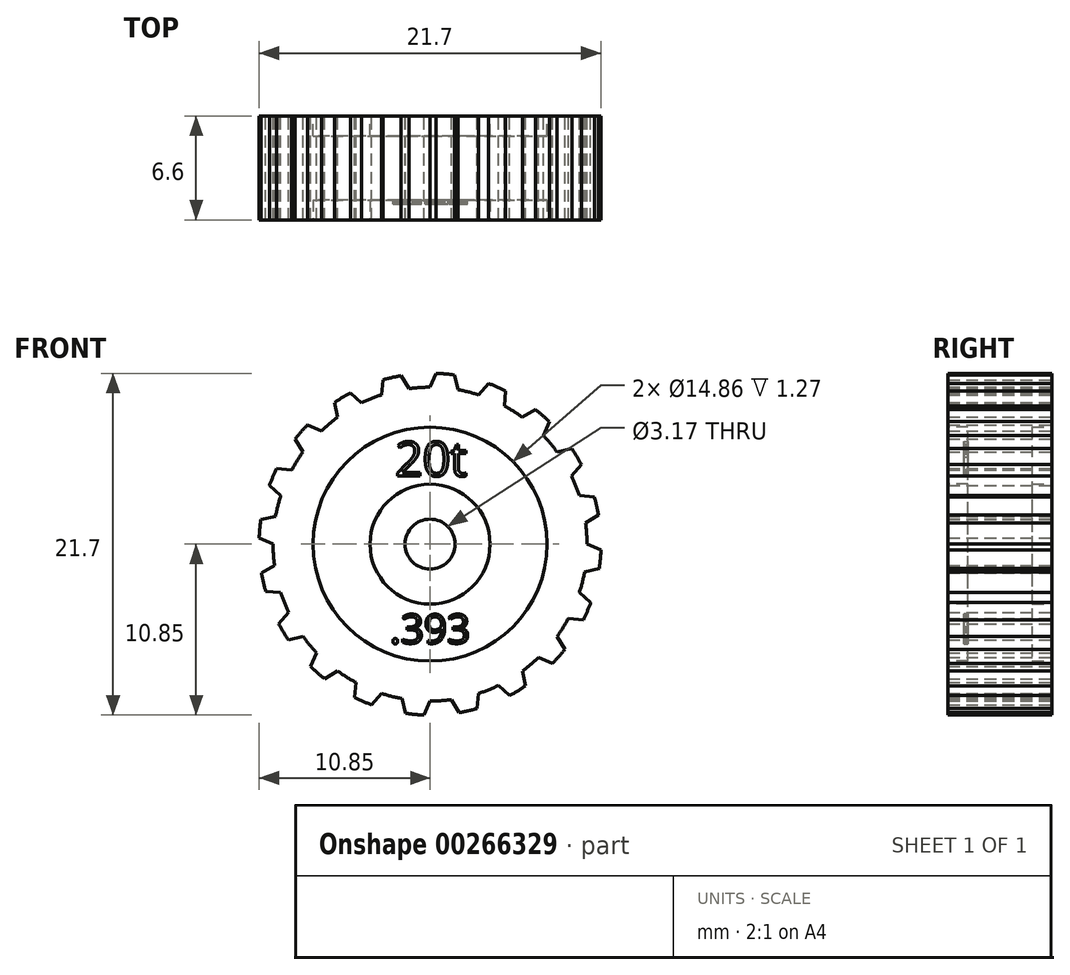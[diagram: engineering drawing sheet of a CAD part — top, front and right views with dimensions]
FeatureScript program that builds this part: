
annotation { "Feature Type Name" : "Feature", "Feature Type Description" : "" }
export const myFeature = defineFeature(function(context is Context, id is Id, definition is map)
    precondition{}
    {
        {
            var Q0;
            Q0=qCreatedBy(makeId("Front.planeOp"),FACE);
            var sketch = newSketch(context, id + "F0", { "sketchPlane" : qUnion([Q0])});
            skCircle(sketch, "E0", {"center": v(0, 0) * mm, "radius": 9.97 * mm});
            skCircle(sketch, "E1", {"center": v(0, 0) * mm, "radius": 1.59 * mm});
            skSolve(sketch);
        }
        {
            var Q0;
            Q0=qSketchRegion(id+"F0",true);
            extrude(context, id + "F1", {"entities" : qUnion([Q0]), "depth" : 6.6 * mm, "offsetDistance" : 25.4 * mm});
        }
        {
            var Q0;
            Q0=makeQuery(id+"F1.opExtrude","CAP_FACE",FACE,{"disambiguationData":[OSD([sQuery(id+"F0.wireOp",EDGE,"E0"),sQuery(id+"F0.wireOp",EDGE,"E1")])],"isStart":false});
            var sketch = newSketch(context, id + "F2", { "sketchPlane" : qUnion([Q0])});
            skCircle(sketch, "E2.0", {"center": v(0, 0) * mm, "radius": 7.43 * mm});
            skCircle(sketch, "E3", {"center": v(0, 0) * mm, "radius": 3.81 * mm});
            skSolve(sketch);
        }
        {
            var Q0;
            Q0=qSketchRegion(id+"F2",true);
            extrude(context, id + "F3", {"entities" : qUnion([Q0]), "operationType" : NewBodyOperationType.REMOVE, "oppositeDirection" : true, "depth" : 1.27 * mm});
        }
        {
            var Q0;
            Q0=makeQuery(id+"F1.opExtrude","CAP_FACE",FACE,{"disambiguationData":[OSD([sQuery(id+"F0.wireOp",EDGE,"E0"),sQuery(id+"F0.wireOp",EDGE,"E1")])],"isStart":true});
            var sketch = newSketch(context, id + "F4", { "sketchPlane" : qUnion([Q0])});
            skCircle(sketch, "E4.0", {"center": v(0, 0) * mm, "radius": 7.43 * mm});
            skCircle(sketch, "E5", {"center": v(0, 0) * mm, "radius": 3.81 * mm});
            skSolve(sketch);
        }
        {
            var Q0;
            Q0=qSketchRegion(id+"F4",true);
            extrude(context, id + "F5", {"entities" : qUnion([Q0]), "operationType" : NewBodyOperationType.REMOVE, "oppositeDirection" : true, "depth" : 1.27 * mm});
        }
        {
            var Q0;
            Q0=makeQuery(id+"F3.boolean.opBoolean","COPY",FACE,{"derivedFrom":makeQuery(id+"F3.opExtrude","CAP_FACE",FACE,{"disambiguationData":[OSD([sQuery(id+"F2.wireOp",EDGE,"E2.0"),sQuery(id+"F2.wireOp",EDGE,"E3")])],"isStart":false})});
            var sketch = newSketch(context, id + "F6", { "sketchPlane" : qUnion([Q0])});
            skText(sketch, "E6", { "text": "20t", "fontName": "OpenSans-Regular.ttf"});
            skText(sketch, "E7", { "text": ".393", "fontName": "OpenSans-Regular.ttf"});
            const initialGuessF6  = {"E6": [-0.00221, 0.00432, 1, 0, 0.0022], "E7": [-0.00255, -0.0063, 1, 0, 0.00185]};
            skSetInitialGuess(sketch, initialGuessF6);
            skSolve(sketch);
        }
        {
            var Q0;
            Q0=qSketchRegion(id+"F6",true);
            extrude(context, id + "F7", {"entities" : qUnion([Q0]), "operationType" : NewBodyOperationType.ADD, "depth" : 0.25 * mm});
        }
        {
            var Q0;
            {var subQ0=sQuery(id+"F0.wireOp",EDGE,"E0");Q0=makeQuery(id+"F5.boolean.opBoolean","SPLIT",FACE,{"disambiguationData":[TD([makeQuery(id+"F1.opExtrude","SWEPT_FACE",FACE,{"disambiguationData":[OSD([subQ0])]})])],"derivedFrom":makeQuery(id+"F1.opExtrude","CAP_FACE",FACE,{"disambiguationData":[OSD([subQ0,sQuery(id+"F0.wireOp",EDGE,"E1")])],"isStart":true})});}
            var sketch = newSketch(context, id + "F8", { "sketchPlane" : qUnion([Q0])});
            skLineSegment(sketch, "E8", {"start": v(0, 0) * mm, "end": v(0, 11.7) * mm, "construction": true});
            skLineSegment(sketch, "E9", {"start": v(0, 0) * mm, "end": v(-3.65, 11.22) * mm, "construction": true});
            skLineSegment(sketch, "E10", {"start": v(0, 0) * mm, "end": v(-1.8, 11.36) * mm, "construction": true});
            skArc(sketch, "E11", {"start": v(-0.38, 10.85) * mm, "mid": v(-0.97, 10.82) * mm, "end": v(-1.56, 10.75) * mm});
            skLineSegment(sketch, "E12", {"start": v(0, 9.97) * mm, "end": v(-0.38, 10.85) * mm});
            skLineSegment(sketch, "E13", {"start": v(-1.56, 10.75) * mm, "end": v(-1.77, 9.81) * mm});
            skLineSegment(sketch, "E14", {"start": v(-1.77, 9.81) * mm, "end": v(0, 9.97) * mm});
            skArc(sketch, "E15.1.0", {"start": v(-3.71, 10.2) * mm, "mid": v(-4.26, 9.99) * mm, "end": v(-4.8, 9.74) * mm});
            skLineSegment(sketch, "E15.1.1", {"start": v(-4.8, 9.74) * mm, "end": v(-4.71, 8.78) * mm});
            skLineSegment(sketch, "E15.1.2", {"start": v(-4.71, 8.78) * mm, "end": v(-3.08, 9.48) * mm});
            skLineSegment(sketch, "E15.1.3", {"start": v(-3.08, 9.48) * mm, "end": v(-3.71, 10.2) * mm});
            skArc(sketch, "E15.2.0", {"start": v(-6.68, 8.56) * mm, "mid": v(-7.14, 8.18) * mm, "end": v(-7.57, 7.78) * mm});
            skLineSegment(sketch, "E15.2.1", {"start": v(-7.57, 7.78) * mm, "end": v(-7.2, 6.9) * mm});
            skLineSegment(sketch, "E15.2.2", {"start": v(-7.2, 6.9) * mm, "end": v(-5.86, 8.07) * mm});
            skLineSegment(sketch, "E15.2.3", {"start": v(-5.86, 8.07) * mm, "end": v(-6.68, 8.56) * mm});
            skArc(sketch, "E16.1.3.0", {"start": v(-9, 6.07) * mm, "mid": v(-9.32, 5.57) * mm, "end": v(-9.6, 5.06) * mm});
            skLineSegment(sketch, "E16.4.3.0", {"start": v(-9.6, 5.06) * mm, "end": v(-8.98, 4.34) * mm});
            skLineSegment(sketch, "E16.7.3.0", {"start": v(-8.98, 4.34) * mm, "end": v(-8.07, 5.86) * mm});
            skLineSegment(sketch, "E16.10.3.0", {"start": v(-8.07, 5.86) * mm, "end": v(-9, 6.07) * mm});
            skArc(sketch, "E16.1.4.0", {"start": v(-10.44, 3) * mm, "mid": v(-10.59, 2.42) * mm, "end": v(-10.7, 1.84) * mm});
            skLineSegment(sketch, "E16.4.4.0", {"start": v(-10.7, 1.84) * mm, "end": v(-9.88, 1.35) * mm});
            skLineSegment(sketch, "E16.7.4.0", {"start": v(-9.88, 1.35) * mm, "end": v(-9.48, 3.08) * mm});
            skLineSegment(sketch, "E16.10.4.0", {"start": v(-9.48, 3.08) * mm, "end": v(-10.44, 3) * mm});
            skArc(sketch, "E16.1.5.0", {"start": v(-10.85, -0.38) * mm, "mid": v(-10.82, -0.97) * mm, "end": v(-10.75, -1.56) * mm});
            skLineSegment(sketch, "E16.4.5.0", {"start": v(-10.75, -1.56) * mm, "end": v(-9.81, -1.77) * mm});
            skLineSegment(sketch, "E16.7.5.0", {"start": v(-9.81, -1.77) * mm, "end": v(-9.97, 0) * mm});
            skLineSegment(sketch, "E16.10.5.0", {"start": v(-9.97, 0) * mm, "end": v(-10.85, -0.38) * mm});
            skArc(sketch, "E16.1.6.0", {"start": v(-10.2, -3.71) * mm, "mid": v(-9.99, -4.26) * mm, "end": v(-9.74, -4.8) * mm});
            skLineSegment(sketch, "E16.4.6.0", {"start": v(-9.74, -4.8) * mm, "end": v(-8.78, -4.71) * mm});
            skLineSegment(sketch, "E16.7.6.0", {"start": v(-8.78, -4.71) * mm, "end": v(-9.48, -3.08) * mm});
            skLineSegment(sketch, "E16.10.6.0", {"start": v(-9.48, -3.08) * mm, "end": v(-10.2, -3.71) * mm});
            skArc(sketch, "E16.1.7.0", {"start": v(-8.56, -6.68) * mm, "mid": v(-8.18, -7.14) * mm, "end": v(-7.78, -7.57) * mm});
            skLineSegment(sketch, "E16.4.7.0", {"start": v(-7.78, -7.57) * mm, "end": v(-6.9, -7.2) * mm});
            skLineSegment(sketch, "E16.7.7.0", {"start": v(-6.9, -7.2) * mm, "end": v(-8.07, -5.86) * mm});
            skLineSegment(sketch, "E16.10.7.0", {"start": v(-8.07, -5.86) * mm, "end": v(-8.56, -6.68) * mm});
            skArc(sketch, "E16.1.8.0", {"start": v(-6.07, -9) * mm, "mid": v(-5.57, -9.32) * mm, "end": v(-5.06, -9.6) * mm});
            skLineSegment(sketch, "E16.4.8.0", {"start": v(-5.06, -9.6) * mm, "end": v(-4.34, -8.98) * mm});
            skLineSegment(sketch, "E16.7.8.0", {"start": v(-4.34, -8.98) * mm, "end": v(-5.86, -8.07) * mm});
            skLineSegment(sketch, "E16.10.8.0", {"start": v(-5.86, -8.07) * mm, "end": v(-6.07, -9) * mm});
            skArc(sketch, "E16.1.9.0", {"start": v(-3, -10.44) * mm, "mid": v(-2.42, -10.59) * mm, "end": v(-1.84, -10.7) * mm});
            skLineSegment(sketch, "E16.4.9.0", {"start": v(-1.84, -10.7) * mm, "end": v(-1.35, -9.88) * mm});
            skLineSegment(sketch, "E16.7.9.0", {"start": v(-1.35, -9.88) * mm, "end": v(-3.08, -9.48) * mm});
            skLineSegment(sketch, "E16.10.9.0", {"start": v(-3.08, -9.48) * mm, "end": v(-3, -10.44) * mm});
            skArc(sketch, "E16.1.10.0", {"start": v(0.38, -10.85) * mm, "mid": v(0.97, -10.82) * mm, "end": v(1.56, -10.75) * mm});
            skLineSegment(sketch, "E16.4.10.0", {"start": v(1.56, -10.75) * mm, "end": v(1.77, -9.81) * mm});
            skLineSegment(sketch, "E16.7.10.0", {"start": v(1.77, -9.81) * mm, "end": v(0, -9.97) * mm});
            skLineSegment(sketch, "E16.10.10.0", {"start": v(0, -9.97) * mm, "end": v(0.38, -10.85) * mm});
            skArc(sketch, "E16.1.11.0", {"start": v(3.71, -10.2) * mm, "mid": v(4.26, -9.99) * mm, "end": v(4.8, -9.74) * mm});
            skLineSegment(sketch, "E16.4.11.0", {"start": v(4.8, -9.74) * mm, "end": v(4.71, -8.78) * mm});
            skLineSegment(sketch, "E16.7.11.0", {"start": v(4.71, -8.78) * mm, "end": v(3.08, -9.48) * mm});
            skLineSegment(sketch, "E16.10.11.0", {"start": v(3.08, -9.48) * mm, "end": v(3.71, -10.2) * mm});
            skArc(sketch, "E16.1.12.0", {"start": v(6.68, -8.56) * mm, "mid": v(7.14, -8.18) * mm, "end": v(7.57, -7.78) * mm});
            skLineSegment(sketch, "E16.4.12.0", {"start": v(7.57, -7.78) * mm, "end": v(7.2, -6.9) * mm});
            skLineSegment(sketch, "E16.7.12.0", {"start": v(7.2, -6.9) * mm, "end": v(5.86, -8.07) * mm});
            skLineSegment(sketch, "E16.10.12.0", {"start": v(5.86, -8.07) * mm, "end": v(6.68, -8.56) * mm});
            skArc(sketch, "E16.1.13.0", {"start": v(9, -6.07) * mm, "mid": v(9.32, -5.57) * mm, "end": v(9.6, -5.06) * mm});
            skLineSegment(sketch, "E16.4.13.0", {"start": v(9.6, -5.06) * mm, "end": v(8.98, -4.34) * mm});
            skLineSegment(sketch, "E16.7.13.0", {"start": v(8.98, -4.34) * mm, "end": v(8.07, -5.86) * mm});
            skLineSegment(sketch, "E16.10.13.0", {"start": v(8.07, -5.86) * mm, "end": v(9, -6.07) * mm});
            skArc(sketch, "E16.1.14.0", {"start": v(10.44, -3) * mm, "mid": v(10.59, -2.42) * mm, "end": v(10.7, -1.84) * mm});
            skLineSegment(sketch, "E16.4.14.0", {"start": v(10.7, -1.84) * mm, "end": v(9.88, -1.35) * mm});
            skLineSegment(sketch, "E16.7.14.0", {"start": v(9.88, -1.35) * mm, "end": v(9.48, -3.08) * mm});
            skLineSegment(sketch, "E16.10.14.0", {"start": v(9.48, -3.08) * mm, "end": v(10.44, -3) * mm});
            skArc(sketch, "E16.1.15.0", {"start": v(10.85, 0.38) * mm, "mid": v(10.82, 0.97) * mm, "end": v(10.75, 1.56) * mm});
            skLineSegment(sketch, "E16.4.15.0", {"start": v(10.75, 1.56) * mm, "end": v(9.81, 1.77) * mm});
            skLineSegment(sketch, "E16.7.15.0", {"start": v(9.81, 1.77) * mm, "end": v(9.97, 0) * mm});
            skLineSegment(sketch, "E16.10.15.0", {"start": v(9.97, 0) * mm, "end": v(10.85, 0.38) * mm});
            skArc(sketch, "E16.1.16.0", {"start": v(10.2, 3.71) * mm, "mid": v(9.99, 4.26) * mm, "end": v(9.74, 4.8) * mm});
            skLineSegment(sketch, "E16.4.16.0", {"start": v(9.74, 4.8) * mm, "end": v(8.78, 4.71) * mm});
            skLineSegment(sketch, "E16.7.16.0", {"start": v(8.78, 4.71) * mm, "end": v(9.48, 3.08) * mm});
            skLineSegment(sketch, "E16.10.16.0", {"start": v(9.48, 3.08) * mm, "end": v(10.2, 3.71) * mm});
            skArc(sketch, "E16.1.17.0", {"start": v(8.56, 6.68) * mm, "mid": v(8.18, 7.14) * mm, "end": v(7.78, 7.57) * mm});
            skLineSegment(sketch, "E16.4.17.0", {"start": v(7.78, 7.57) * mm, "end": v(6.9, 7.2) * mm});
            skLineSegment(sketch, "E16.7.17.0", {"start": v(6.9, 7.2) * mm, "end": v(8.07, 5.86) * mm});
            skLineSegment(sketch, "E16.10.17.0", {"start": v(8.07, 5.86) * mm, "end": v(8.56, 6.68) * mm});
            skArc(sketch, "E16.1.18.0", {"start": v(6.07, 9) * mm, "mid": v(5.57, 9.32) * mm, "end": v(5.06, 9.6) * mm});
            skLineSegment(sketch, "E16.4.18.0", {"start": v(5.06, 9.6) * mm, "end": v(4.34, 8.98) * mm});
            skLineSegment(sketch, "E16.7.18.0", {"start": v(4.34, 8.98) * mm, "end": v(5.86, 8.07) * mm});
            skLineSegment(sketch, "E16.10.18.0", {"start": v(5.86, 8.07) * mm, "end": v(6.07, 9) * mm});
            skArc(sketch, "E16.1.19.0", {"start": v(3, 10.44) * mm, "mid": v(2.42, 10.59) * mm, "end": v(1.84, 10.7) * mm});
            skLineSegment(sketch, "E16.4.19.0", {"start": v(1.84, 10.7) * mm, "end": v(1.35, 9.88) * mm});
            skLineSegment(sketch, "E16.7.19.0", {"start": v(1.35, 9.88) * mm, "end": v(3.08, 9.48) * mm});
            skLineSegment(sketch, "E16.10.19.0", {"start": v(3.08, 9.48) * mm, "end": v(3, 10.44) * mm});
            skSolve(sketch);
        }
        {
            var Q0;
            Q0=qSketchRegion(id+"F8",true);
            var Q1;
            {var subQ0=sQuery(id+"F0.wireOp",EDGE,"E0");Q1=makeQuery(id+"F3.boolean.opBoolean","SPLIT",FACE,{"disambiguationData":[TD([makeQuery(id+"F1.opExtrude","SWEPT_FACE",FACE,{"disambiguationData":[OSD([subQ0])]})])],"derivedFrom":makeQuery(id+"F1.opExtrude","CAP_FACE",FACE,{"disambiguationData":[OSD([subQ0,sQuery(id+"F0.wireOp",EDGE,"E1")])],"isStart":false})});}
            extrude(context, id + "F9", {"entities" : qUnion([Q0]), "operationType" : NewBodyOperationType.ADD, "endBound" : BoundingType.UP_TO_SURFACE, "oppositeDirection" : true, "endBoundEntityFace" : qUnion([Q1]), "depth" : 25.4 * mm});
        }
    });
